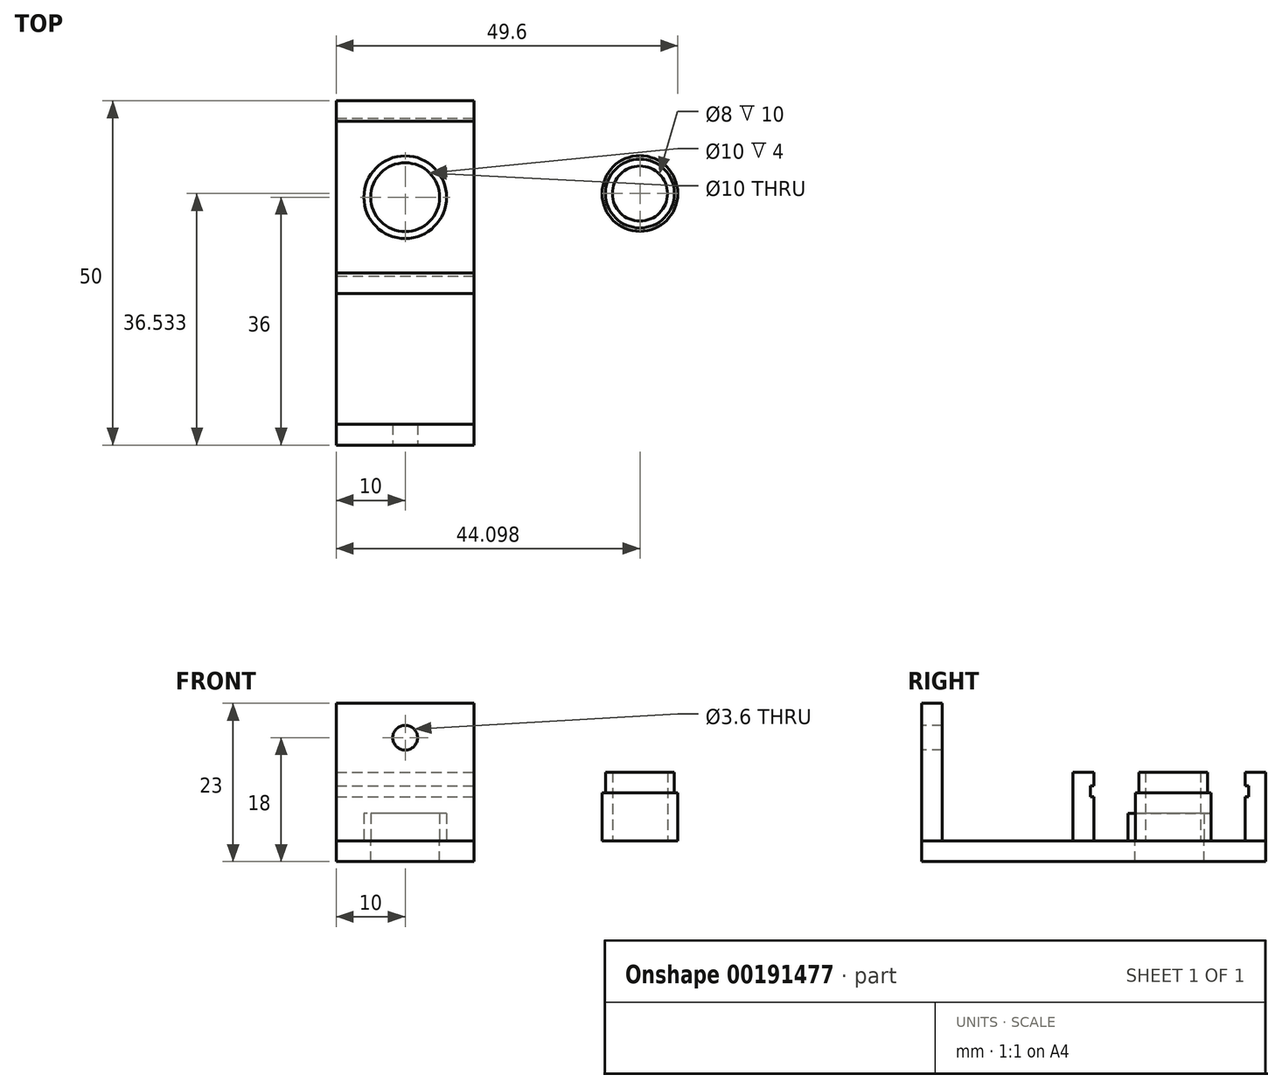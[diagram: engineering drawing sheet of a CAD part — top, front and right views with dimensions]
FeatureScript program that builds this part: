
annotation { "Feature Type Name" : "Feature", "Feature Type Description" : "" }
export const myFeature = defineFeature(function(context is Context, id is Id, definition is map)
    precondition{}
    {
        {
            var Q0;
            Q0=qCreatedBy(makeId("Top.planeOp"),FACE);
            var sketch = newSketch(context, id + "F0", { "sketchPlane" : qUnion([Q0])});
            skLineSegment(sketch, "E0.bottom", {"start": v(-10, 0) * mm, "end": v(10, 0) * mm});
            skLineSegment(sketch, "E0.top", {"start": v(-10, 50) * mm, "end": v(10, 50) * mm});
            skLineSegment(sketch, "E0.left", {"start": v(-10, 0) * mm, "end": v(-10, 50) * mm});
            skLineSegment(sketch, "E0.right", {"start": v(10, 0) * mm, "end": v(10, 50) * mm});
            skLineSegment(sketch, "E1", {"start": v(-10, 3) * mm, "end": v(10, 3) * mm});
            skLineSegment(sketch, "E2", {"start": v(-10, 47) * mm, "end": v(10, 47) * mm});
            skLineSegment(sketch, "E3", {"start": v(-10, 25) * mm, "end": v(10, 25) * mm});
            skLineSegment(sketch, "E4", {"start": v(-10, 22) * mm, "end": v(10, 22) * mm});
            skPoint(sketch, "E5", {"position": v(0, 0) * mm});
            skLineSegment(sketch, "E6", {"start": v(0, 47) * mm, "end": v(0, 25) * mm, "construction": true});
            skCircle(sketch, "E7", {"center": v(0, 36) * mm, "radius": 5 * mm});
            skCircle(sketch, "E8", {"center": v(0, 36) * mm, "radius": 6 * mm});
            skSolve(sketch);
        }
        {
            var Q0;
            {var subQ0=sQuery(id+"F0.wireOp",EDGE,"E0.bottom");Q0=makeQuery(id+"F0.imprint","IMPRINT",FACE,{"disambiguationData":[TD([[makeQuery(id+"F0.imprint","IMPRINT",EDGE,{"derivedFrom":subQ0}),1.0]])]});}
            var Q1;
            {var subQ0=sQuery(id+"F0.wireOp",EDGE,"E3");Q1=makeQuery(id+"F0.imprint","IMPRINT",FACE,{"disambiguationData":[TD([[makeQuery(id+"F0.imprint","IMPRINT",EDGE,{"derivedFrom":subQ0}),-1.0]])]});}
            var Q2;
            {var subQ0=sQuery(id+"F0.wireOp",EDGE,"E0.top");Q2=makeQuery(id+"F0.imprint","IMPRINT",FACE,{"disambiguationData":[TD([[makeQuery(id+"F0.imprint","IMPRINT",EDGE,{"derivedFrom":subQ0}),-1.0]])]});}
            extrude(context, id + "F1", {"entities" : qUnion([Q0, Q1, Q2]), "depth" : 10 * mm});
        }
        {
            var Q0;
            Q0=makeQuery(id+"F0.imprint","IMPRINT",FACE,{"disambiguationData":[TD([[makeQuery(id+"F0.imprint","IMPRINT",EDGE,{"derivedFrom":sQuery(id+"F0.wireOp",EDGE,"E7")}),-1.0]])]});
            extrude(context, id + "F2", {"entities" : qUnion([Q0]), "depth" : 4 * mm});
        }
        {
            var Q0;
            {var subQ0=sQuery(id+"F0.wireOp",EDGE,"E0.top");Q0=makeQuery(id+"F0.imprint","IMPRINT",FACE,{"disambiguationData":[TD([[makeQuery(id+"F0.imprint","IMPRINT",EDGE,{"derivedFrom":subQ0}),-1.0]])]});}
            var Q1;
            {var subQ1=sQuery(id+"F0.wireOp",EDGE,"E2");Q1=makeQuery(id+"F0.imprint","IMPRINT",FACE,{"disambiguationData":[TD([[makeQuery(id+"F0.imprint","IMPRINT",EDGE,{"derivedFrom":subQ1}),-1.0]])]});}
            var Q2;
            Q2=makeQuery(id+"F0.imprint","IMPRINT",FACE,{"disambiguationData":[TD([[makeQuery(id+"F0.imprint","IMPRINT",EDGE,{"derivedFrom":sQuery(id+"F0.wireOp",EDGE,"E7")}),-1.0]])]});
            var Q3;
            {var subQ0=sQuery(id+"F0.wireOp",EDGE,"E3");Q3=makeQuery(id+"F0.imprint","IMPRINT",FACE,{"disambiguationData":[TD([[makeQuery(id+"F0.imprint","IMPRINT",EDGE,{"derivedFrom":subQ0}),-1.0]])]});}
            var Q4;
            {var subQ0=sQuery(id+"F0.wireOp",EDGE,"E1");Q4=makeQuery(id+"F0.imprint","IMPRINT",FACE,{"disambiguationData":[TD([[makeQuery(id+"F0.imprint","IMPRINT",EDGE,{"derivedFrom":subQ0}),1.0]])]});}
            var Q5;
            {var subQ0=sQuery(id+"F0.wireOp",EDGE,"E0.bottom");Q5=makeQuery(id+"F0.imprint","IMPRINT",FACE,{"disambiguationData":[TD([[makeQuery(id+"F0.imprint","IMPRINT",EDGE,{"derivedFrom":subQ0}),1.0]])]});}
            extrude(context, id + "F3", {"entities" : qUnion([Q0, Q1, Q2, Q3, Q4, Q5]), "oppositeDirection" : true, "depth" : 3 * mm});
        }
        {
            var Q0;
            Q0=makeQuery(id+"F1.opExtrude","SWEPT_FACE",FACE,{"disambiguationData":[OSD([sQuery(id+"F0.wireOp",EDGE,"E2")])]});
            var sketch = newSketch(context, id + "F4", { "sketchPlane" : qUnion([Q0])});
            skLineSegment(sketch, "E9", {"start": v(-10, 8) * mm, "end": v(10, 8) * mm});
            skLineSegment(sketch, "E10", {"start": v(-10, 6.4) * mm, "end": v(10, 6.4) * mm});
            skSolve(sketch);
        }
        {
            var Q0;
            Q0 = qSketchRegion(id + "F4", true);
            var Q1;
            {var subQ0=sQuery(id+"F4.wireOp",EDGE,"E9");Q1=makeQuery(id+"F4.imprint","IMPRINT",FACE,{"disambiguationData":[TD([[makeQuery(id+"F4.imprint","IMPRINT",EDGE,{"derivedFrom":subQ0}),-1.0]])]});}
            extrude(context, id + "F5", {"entities" : qUnion([Q0, Q1]), "operationType" : NewBodyOperationType.REMOVE, "oppositeDirection" : true, "depth" : 0.5 * mm});
        }
        {
            var Q0;
            Q0=makeQuery(id+"F1.opExtrude","SWEPT_FACE",FACE,{"disambiguationData":[OSD([sQuery(id+"F0.wireOp",EDGE,"E3")])]});
            var sketch = newSketch(context, id + "F6", { "sketchPlane" : qUnion([Q0])});
            skLineSegment(sketch, "E11", {"start": v(-10, 8) * mm, "end": v(10, 8) * mm});
            skLineSegment(sketch, "E12", {"start": v(-10, 6.4) * mm, "end": v(10, 6.4) * mm});
            skSolve(sketch);
        }
        {
            var Q0;
            Q0 = qSketchRegion(id + "F6", true);
            var Q1;
            {var subQ0=sQuery(id+"F6.wireOp",EDGE,"E11");Q1=makeQuery(id+"F6.imprint","IMPRINT",FACE,{"disambiguationData":[TD([[makeQuery(id+"F6.imprint","IMPRINT",EDGE,{"derivedFrom":subQ0}),-1.0]])]});}
            extrude(context, id + "F7", {"entities" : qUnion([Q0, Q1]), "operationType" : NewBodyOperationType.REMOVE, "oppositeDirection" : true, "depth" : 0.5 * mm});
        }
        {
            var Q0;
            Q0=makeQuery(id+"F1.opExtrude","CAP_FACE",FACE,{"disambiguationData":[OSD([sQuery(id+"F0.wireOp",EDGE,"E0.bottom"),sQuery(id+"F0.wireOp",EDGE,"E0.left"),sQuery(id+"F0.wireOp",EDGE,"E0.right"),sQuery(id+"F0.wireOp",EDGE,"E1")])],"isStart":false});
            extrude(context, id + "F8", {"entities" : qUnion([Q0]), "operationType" : NewBodyOperationType.ADD, "depth" : 10 * mm});
        }
        {
            var Q0;
            Q0=qCreatedBy(makeId("Front.planeOp"),FACE);
            var sketch = newSketch(context, id + "F9", { "sketchPlane" : qUnion([Q0])});
            skCircle(sketch, "E13", {"center": v(0, 15) * mm, "radius": 1.8 * mm});
            skSolve(sketch);
        }
        {
            var Q0;
            Q0=makeQuery(id+"F9.imprint","IMPRINT",FACE,{"disambiguationData":[TD([[makeQuery(id+"F9.imprint","IMPRINT",EDGE,{"derivedFrom":sQuery(id+"F9.wireOp",EDGE,"E13")}),1.0]])]});
            extrude(context, id + "F10", {"entities" : qUnion([Q0]), "operationType" : NewBodyOperationType.REMOVE, "endBound" : BoundingType.THROUGH_ALL, "oppositeDirection" : true, "depth" : 25 * mm});
        }
        {
            var Q0;
            Q0=qCreatedBy(makeId("Top.planeOp"),FACE);
            var sketch = newSketch(context, id + "F11", { "sketchPlane" : qUnion([Q0])});
            skCircle(sketch, "E14", {"center": v(34.1, 36.53) * mm, "radius": 5 * mm});
            skCircle(sketch, "E15", {"center": v(34.1, 36.53) * mm, "radius": 4 * mm});
            skCircle(sketch, "E16", {"center": v(34.1, 36.53) * mm, "radius": 5.5 * mm});
            skSolve(sketch);
        }
        {
            var Q0;
            Q0=makeQuery(id+"F11.imprint","IMPRINT",FACE,{"disambiguationData":[TD([[makeQuery(id+"F11.imprint","IMPRINT",EDGE,{"derivedFrom":sQuery(id+"F11.wireOp",EDGE,"E14")}),1.0]])]});
            extrude(context, id + "F12", {"entities" : qUnion([Q0]), "depth" : 10 * mm});
        }
        {
            var Q0;
            Q0=sQuery(id+"F11.wireOp",EDGE,"E16");
            var Q1;
            Q1=sQuery(id+"F11.wireOp",EDGE,"E14");
            extrude(context, id + "F13", {"bodyType" : ToolBodyType.SURFACE, "surfaceEntities" : qUnion([Q0, Q1]), "depth" : 6 * mm});
        }
        {
            var Q0;
            Q0=makeQuery(id+"F13.opExtrude","SWEPT_BODY",BODY,{"disambiguationData":[OSD([sQuery(id+"F11.wireOp",EDGE,"E14")])]});
            var Q1;
            Q1=makeQuery(id+"F13.opExtrude","SWEPT_BODY",BODY,{"disambiguationData":[OSD([sQuery(id+"F11.wireOp",EDGE,"E16")])]});
            var Q2;
            Q2=makeQuery(id+"F12.opExtrude","SWEPT_BODY",BODY,{"disambiguationData":[OSD([sQuery(id+"F11.wireOp",EDGE,"E14"),sQuery(id+"F11.wireOp",EDGE,"E15")])]});
            deleteBodies(context, id + "F14", {"entities" : qUnion([Q0, Q1, Q2])});
        }
        {
            var Q0;
            Q0=makeQuery(id+"F11.imprint","IMPRINT",FACE,{"disambiguationData":[TD([[makeQuery(id+"F11.imprint","IMPRINT",EDGE,{"derivedFrom":sQuery(id+"F11.wireOp",EDGE,"E14")}),-1.0]])]});
            var Q1;
            Q1=makeQuery(id+"F11.imprint","IMPRINT",FACE,{"disambiguationData":[TD([[makeQuery(id+"F11.imprint","IMPRINT",EDGE,{"derivedFrom":sQuery(id+"F11.wireOp",EDGE,"E14")}),1.0]])]});
            extrude(context, id + "F15", {"entities" : qUnion([Q0, Q1]), "depth" : 7 * mm});
        }
        {
            var Q0;
            Q0=makeQuery(id+"F11.imprint","IMPRINT",FACE,{"disambiguationData":[TD([[makeQuery(id+"F11.imprint","IMPRINT",EDGE,{"derivedFrom":sQuery(id+"F11.wireOp",EDGE,"E14")}),1.0]])]});
            extrude(context, id + "F16", {"entities" : qUnion([Q0]), "operationType" : NewBodyOperationType.ADD, "depth" : 10 * mm});
        }
    });
